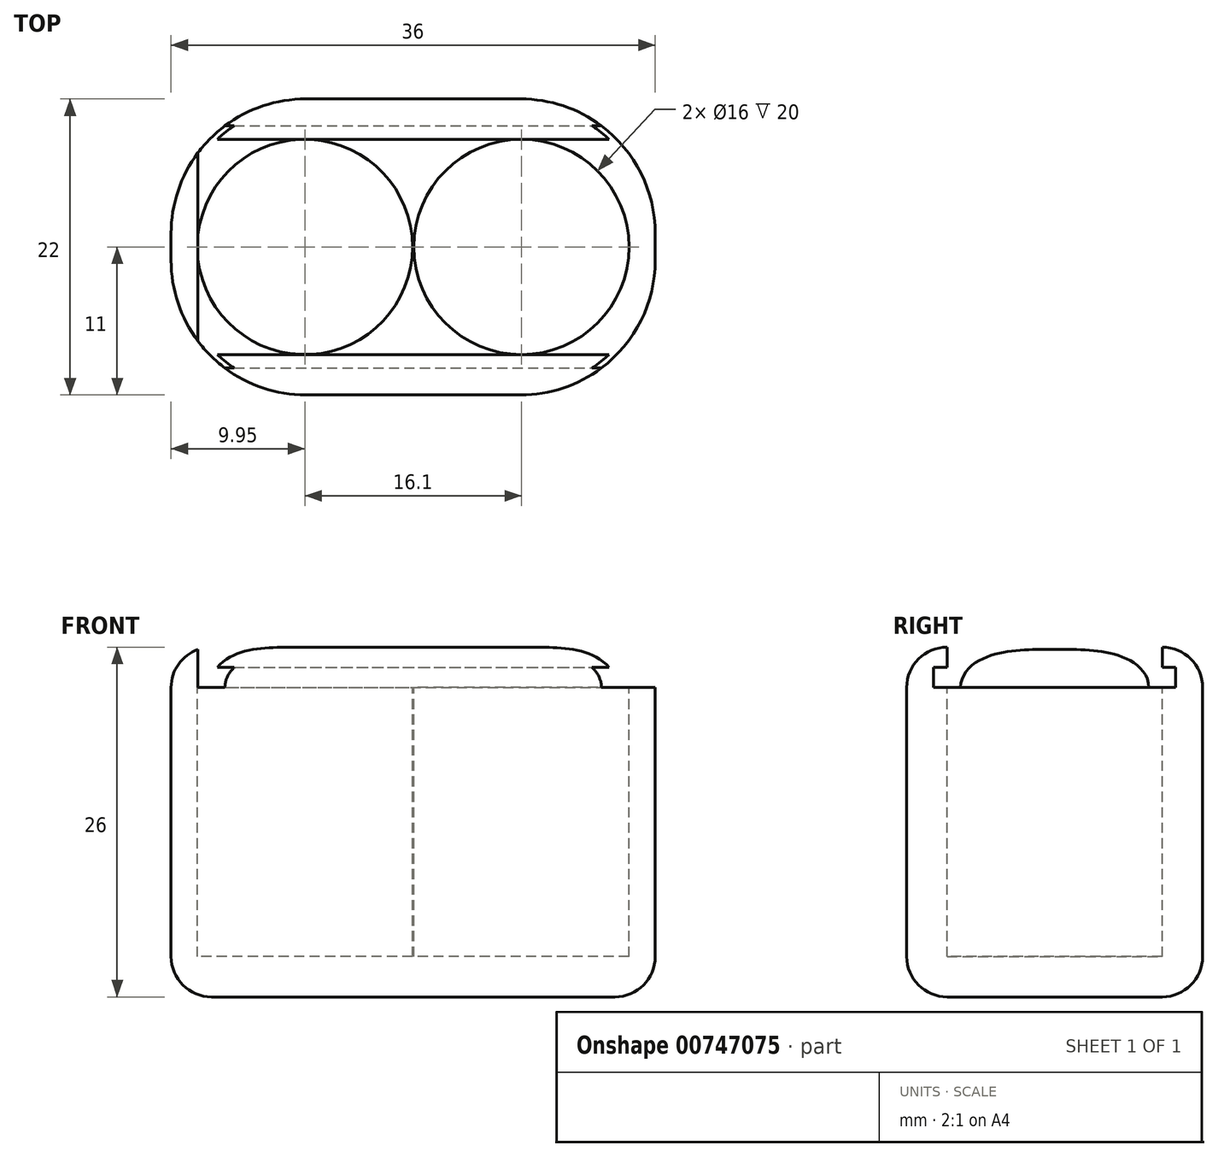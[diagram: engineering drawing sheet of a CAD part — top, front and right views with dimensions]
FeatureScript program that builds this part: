
annotation { "Feature Type Name" : "Feature", "Feature Type Description" : "" }
export const myFeature = defineFeature(function(context is Context, id is Id, definition is map)
    precondition{}
    {
        {
            var Q0;
            Q0=qCreatedBy(makeId("Top.planeOp"),FACE);
            var sketch = newSketch(context, id + "F0", { "sketchPlane" : qUnion([Q0])});
            skLineSegment(sketch, "E0.bottom", {"start": v(8, -11) * mm, "end": v(-8, -11) * mm});
            skLineSegment(sketch, "E0.top", {"start": v(8, 11) * mm, "end": v(-8, 11) * mm});
            skLineSegment(sketch, "E0.left", {"start": v(18, -1) * mm, "end": v(18, 1) * mm});
            skLineSegment(sketch, "E0.right", {"start": v(-18, -1) * mm, "end": v(-18, 1) * mm});
            skPoint(sketch, "E0.middle", {"position": v(0, 0) * mm});
            skPoint(sketch, "E1.visualSharp", {"position": v(-18, 11) * mm});
            skArc(sketch, "E1.filletArc", {"start": v(-8, 11) * mm, "mid": v(-15.07, 8.07) * mm, "end": v(-18, 1) * mm});
            skPoint(sketch, "E2.visualSharp", {"position": v(-18, -11) * mm});
            skArc(sketch, "E2.filletArc", {"start": v(-18, -1) * mm, "mid": v(-15.07, -8.07) * mm, "end": v(-8, -11) * mm});
            skPoint(sketch, "E3.visualSharp", {"position": v(18, -11) * mm});
            skArc(sketch, "E3.filletArc", {"start": v(8, -11) * mm, "mid": v(15.07, -8.07) * mm, "end": v(18, -1) * mm});
            skPoint(sketch, "E4.visualSharp", {"position": v(18, 11) * mm});
            skArc(sketch, "E4.filletArc", {"start": v(18, 1) * mm, "mid": v(15.07, 8.07) * mm, "end": v(8, 11) * mm});
            skSolve(sketch);
        }
        {
            var Q0;
            Q0=makeQuery(id+"F0.imprint","IMPRINT",FACE,{"disambiguationData":[TD([[makeQuery(id+"F0.imprint","IMPRINT",EDGE,{"derivedFrom":sQuery(id+"F0.wireOp",EDGE,"E0.bottom")}),-1.0]])]});
            extrude(context, id + "F1", {"entities" : qUnion([Q0]), "depth" : 26 * mm, "offsetDistance" : 25 * mm});
        }
        {
            var Q0;
            Q0=makeQuery(id+"F1.opExtrude","CAP_FACE",FACE,{"disambiguationData":[OSD([sQuery(id+"F0.wireOp",EDGE,"E0.bottom"),sQuery(id+"F0.wireOp",EDGE,"E0.top"),sQuery(id+"F0.wireOp",EDGE,"E0.left"),sQuery(id+"F0.wireOp",EDGE,"E0.right"),sQuery(id+"F0.wireOp",EDGE,"E1.filletArc"),sQuery(id+"F0.wireOp",EDGE,"E2.filletArc"),sQuery(id+"F0.wireOp",EDGE,"E3.filletArc"),sQuery(id+"F0.wireOp",EDGE,"E4.filletArc")])],"isStart":true});
            fillet(context, id + "F2", {"entities" : qUnion([Q0]), "radius" : 3 * mm, "tangentPropagation" : true, "allowEdgeOverflow" : false});
        }
        {
            var Q0;
            Q0=makeQuery(id+"F1.opExtrude","CAP_FACE",FACE,{"disambiguationData":[OSD([sQuery(id+"F0.wireOp",EDGE,"E0.bottom"),sQuery(id+"F0.wireOp",EDGE,"E0.top"),sQuery(id+"F0.wireOp",EDGE,"E1.filletArc"),sQuery(id+"F0.wireOp",EDGE,"E2.filletArc"),sQuery(id+"F0.wireOp",EDGE,"E3.filletArc"),sQuery(id+"F0.wireOp",EDGE,"E4.filletArc")])],"isStart":false});
            var sketch = newSketch(context, id + "F3", { "sketchPlane" : qUnion([Q0])});
            skLineSegment(sketch, "E5", {"start": v(-8.05, 0) * mm, "end": v(8.05, 0) * mm, "construction": true});
            skCircle(sketch, "E6", {"center": v(-8.05, 0) * mm, "radius": 8 * mm});
            skCircle(sketch, "E7", {"center": v(8.05, 0) * mm, "radius": 8 * mm});
            skSolve(sketch);
        }
        {
            var Q0;
            Q0=makeQuery(id+"F3.imprint","IMPRINT",FACE,{"disambiguationData":[TD([[makeQuery(id+"F3.imprint","IMPRINT",EDGE,{"derivedFrom":sQuery(id+"F3.wireOp",EDGE,"E7")}),1.0]])]});
            var Q1;
            Q1=makeQuery(id+"F3.imprint","IMPRINT",FACE,{"disambiguationData":[TD([[makeQuery(id+"F3.imprint","IMPRINT",EDGE,{"derivedFrom":sQuery(id+"F3.wireOp",EDGE,"E6")}),1.0]])]});
            extrude(context, id + "F4", {"entities" : qUnion([Q0, Q1]), "operationType" : NewBodyOperationType.REMOVE, "oppositeDirection" : true, "depth" : 23 * mm, "offsetDistance" : 25 * mm});
        }
        {
            var Q0;
            Q0=makeQuery(id+"F3.imprint","IMPRINT",FACE,{"disambiguationData":[TD([[makeQuery(id+"F3.imprint","IMPRINT",EDGE,{"derivedFrom":sQuery(id+"F3.wireOp",EDGE,"E6")}),-1.0]])]});
            cPlane(context, id + "F5", {"entities" : qUnion([Q0]), "cplaneType" : CPlaneType.OFFSET, "offset" : 3 * mm, "oppositeDirection" : true, "width" : 150 * mm, "height" : 150 * mm});
        }
        {
            var Q0;
            Q0=qCreatedBy(id+"F5.planeOp",FACE);
            var sketch = newSketch(context, id + "F6", { "sketchPlane" : qUnion([Q0])});
            skCircle(sketch, "E8.0", {"center": v(-8.05, 0) * mm, "radius": 8 * mm});
            skCircle(sketch, "E9.0", {"center": v(8.05, 0) * mm, "radius": 8 * mm});
            skSolve(sketch);
        }
        {
            var Q0;
            Q0 = qSketchRegion(id + "F6", true);
            var Q1;
            Q1=makeQuery(id+"F1.opExtrude","CAP_FACE",FACE,{"disambiguationData":[OSD([sQuery(id+"F0.wireOp",EDGE,"E0.bottom"),sQuery(id+"F0.wireOp",EDGE,"E0.top"),sQuery(id+"F0.wireOp",EDGE,"E0.left"),sQuery(id+"F0.wireOp",EDGE,"E0.right"),sQuery(id+"F0.wireOp",EDGE,"E1.filletArc"),sQuery(id+"F0.wireOp",EDGE,"E2.filletArc"),sQuery(id+"F0.wireOp",EDGE,"E3.filletArc"),sQuery(id+"F0.wireOp",EDGE,"E4.filletArc")])],"isStart":false});
            extrude(context, id + "F7", {"entities" : qUnion([Q0]), "operationType" : NewBodyOperationType.ADD, "endBound" : BoundingType.UP_TO_SURFACE, "depth" : 2 * mm, "endBoundEntityFace" : qUnion([Q1]), "offsetDistance" : 25 * mm});
        }
        {
            var Q0;
            Q0=makeQuery(id+"F7.boolean.opBoolean","MERGE",FACE,{"derivedFrom":[makeQuery(id+"F1.opExtrude","CAP_FACE",FACE,{"disambiguationData":[OSD([sQuery(id+"F0.wireOp",EDGE,"E0.bottom"),sQuery(id+"F0.wireOp",EDGE,"E0.top"),sQuery(id+"F0.wireOp",EDGE,"E0.left"),sQuery(id+"F0.wireOp",EDGE,"E0.right"),sQuery(id+"F0.wireOp",EDGE,"E1.filletArc"),sQuery(id+"F0.wireOp",EDGE,"E2.filletArc"),sQuery(id+"F0.wireOp",EDGE,"E3.filletArc"),sQuery(id+"F0.wireOp",EDGE,"E4.filletArc")])],"isStart":false}),makeQuery(id+"F7.opExtrude","CAP_FACE",FACE,{"disambiguationData":[OSD([sQuery(id+"F6.wireOp",EDGE,"E8.0")])],"isStart":false}),makeQuery(id+"F7.opExtrude","CAP_FACE",FACE,{"disambiguationData":[OSD([sQuery(id+"F6.wireOp",EDGE,"E9.0")])],"isStart":false})]});
            fillet(context, id + "F8", {"entities" : qUnion([Q0]), "radius" : 3 * mm, "tangentPropagation" : true, "allowEdgeOverflow" : false});
        }
        {
            var Q0;
            Q0=makeQuery(id+"F1.opExtrude","SWEPT_FACE",FACE,{"disambiguationData":[OSD([sQuery(id+"F0.wireOp",EDGE,"E0.left")])]});
            cPlane(context, id + "F9", {"entities" : qUnion([Q0]), "cplaneType" : CPlaneType.OFFSET, "offset" : 1 * mm, "width" : 150 * mm, "height" : 150 * mm});
        }
        {
            var Q0;
            Q0=qCreatedBy(id+"F9.planeOp",FACE);
            var sketch = newSketch(context, id + "F10", { "sketchPlane" : qUnion([Q0])});
            skLineSegment(sketch, "E10.0", {"start": v(-8, 23) * mm, "end": v(-8, 23) * mm});
            skLineSegment(sketch, "E11.0.1", {"start": v(-8, 26) * mm, "end": v(-1, 26) * mm});
            skLineSegment(sketch, "E11.0.2", {"start": v(-1, 26) * mm, "end": v(1, 26) * mm});
            skLineSegment(sketch, "E11.0.3", {"start": v(1, 26) * mm, "end": v(8, 26) * mm});
            skLineSegment(sketch, "E11.0.5", {"start": v(8, 26) * mm, "end": v(1, 26) * mm});
            skLineSegment(sketch, "E11.0.6", {"start": v(1, 26) * mm, "end": v(1, 26) * mm});
            skLineSegment(sketch, "E11.0.7", {"start": v(-1, 26) * mm, "end": v(-8, 26) * mm});
            skLineSegment(sketch, "E12", {"start": v(-8, 26) * mm, "end": v(-8, 24.5) * mm});
            skLineSegment(sketch, "E13", {"start": v(-8, 24.5) * mm, "end": v(-9, 24.5) * mm});
            skLineSegment(sketch, "E14", {"start": v(-9, 24.5) * mm, "end": v(-9, 23) * mm});
            skLineSegment(sketch, "E15", {"start": v(-9, 23) * mm, "end": v(-8, 23) * mm});
            skPoint(sketch, "E16", {"position": v(0, 26) * mm});
            skLineSegment(sketch, "E17", {"start": v(0, 29.88) * mm, "end": v(0, 0) * mm, "construction": true});
            skLineSegment(sketch, "E18.MirrorCS", {"start": v(8, 26) * mm, "end": v(8, 24.5) * mm});
            skLineSegment(sketch, "E19.MirrorCS", {"start": v(8, 24.5) * mm, "end": v(9, 24.5) * mm});
            skLineSegment(sketch, "E20.MirrorCS", {"start": v(9, 24.5) * mm, "end": v(9, 23) * mm});
            skLineSegment(sketch, "E21.MirrorCS", {"start": v(9, 23) * mm, "end": v(8, 23) * mm});
            skLineSegment(sketch, "E22", {"start": v(-8, 23) * mm, "end": v(8, 23) * mm});
            skLineSegment(sketch, "E23", {"start": v(8, 23) * mm, "end": v(8, 23) * mm});
            skLineSegment(sketch, "E24", {"start": v(1, 26) * mm, "end": v(-1, 26) * mm});
            skLineSegment(sketch, "E25", {"start": v(-1, 26) * mm, "end": v(-1, 26) * mm});
            skSolve(sketch);
        }
        {
            var Q0;
            Q0 = qSketchRegion(id + "F10", true);
            extrude(context, id + "F11", {"entities" : qUnion([Q0]), "operationType" : NewBodyOperationType.REMOVE, "oppositeDirection" : true, "depth" : 35 * mm, "offsetDistance" : 25 * mm});
        }
    });
